# Revit family: BidetMixer_Countertop_WithPopup_Vitra_XLineSeries_A42323
name_source: partatom
category: Plumbing Fixtures
revit_build: Autodesk Revit 2017 (Build: 20160225_1515(x64)
units: mm (PartAtom-declared; Revit-internal decimal feet)

## family parameters
Cut with Voids When Loaded = No
Host = Face
OmniClass Number = 23.45.55.17
OmniClass Title = Mixing Faucets
Part Type = Normal
Room Calculation Point = No
Round Connector Dimension = Use Diameter
Shared = Yes

## types (7) — shared parameters
BIMobject category = Taps & Mixers
CW Connection = Yes
Default Elevation = 850 mm  [stored 2.78871 ft]
Depth(mm) = 167 mm  [stored 0.5479 ft]
Description = X-Line Bidet Mixer
Design country = Turkey
HW Connection = Yes
Height(mm) = 190 mm
Hot Water Supply (max.) = 80 °C
Hot Water temperature, factory set to = 38 °C
IFC Classification = Sanitary Terminal
Main Material = Brass
Manufacturer = Vitra
Manufacturer name = Vitra
Masterformat 2014 Code = 22 40 00
Masterformat 2014 Description = Plumbing Fixtures
Min. flow pressure of = 0.5 bar
MountingType = Countertop
NBS Referans Code = 45-35-70/371
NBS Referans Description = Water supply fittings for wash basins and troughs
Nominal height = 0.000
Nominal width = 0.000
Number Of Connections = 2 mm  [stored 0.00656168 ft]
OmniClass Code = 23.45.55.17
OmniClass Description = Mixing Faucets
Product Properties = Extra Water Saving, Green Building Certification, Energy Saving
Product Type = Bidet Mixer
Product certification = https://vitraglobal.com
Product family = X-Line
Product group = X-Line Bidet Mixer
Range of Hot Water Supply = 5 - 65 °C
Range of flow pressure = 1 - 5 bar
Test Pressure = 16 bar
UNSPSC Code = 301815
URL = https://vitraglobal.com
Uniclass 1.4 Code = L725111
Uniclass 1.4 Description = Mixer taps
Uniclass 2.0 Code = Pr_40_30_96_98
Uniclass 2.0 Description = Washbasin Tap
Uniclass 2015 Code = Pr_40_20_87_98
Uniclass 2015 Name = Washbasin Tap
Uniformat II Code = 22 40 00
Uniformat II Description = Plumbing Fixture
Weight Net (kg) = 2.020
Width(mm) = 50 mm  [stored 0.164042 ft]
Youtube = https://www.youtube.com
zero-valued in all types: Cost

## per-type parameters (varying)
| type | Article No. (default) | Brand | Coating Material | Color | Connection Diameter (mm) | Flow Rate(L/min. - 3 bar) | Installation instructions | Model | Product Guid | Product SKU | Product data url | Technical description | Warranty Period (Year) |
| BidetMixer-XLineSeries(Chrome)-A42323 | A42323 | Artema | Chrome | Chrome | 10 mm  [stored 0.0328084 ft] | 5L/min. |  | A42323 |  | A42323 | https://www.vitra.com.tr | https://www.vitra.com.tr | 10 Years |
| BidetMixer-XLineSeries(Gold)-A4232323 | A4232323 | Artema | Gold | Gold | 10 mm  [stored 0.0328084 ft] | 5L/min. |  | A4232323 |  | A4232323 | https://www.vitra.com.tr | https://www.vitra.com.tr | 10 Years |
| BidetMixer-XLineSeries(Chrome)-A42323EXP | A42323EXP | Vitra | Chrome | Chrome | 10 mm  [stored 0.0328084 ft] | 3L/min. | https://cdn.vitra.com.tr | A42323EXP | https://cdn.vitra.com.tr | A42323EXP | https://www.vitraglobal.com | https://www.vitraglobal.com | 7 Years |
| BidetMixer-XLineSeries(Gold)-A4232323EXP | A4232323EXP | Vitra | Gold | Gold | 10 mm  [stored 0.0328084 ft] | 3L/min. | https://cdn.vitra.com.tr | A4232323EXP | https://cdn.vitra.com.tr | A4232323EXP | https://www.vitraglobal.com | https://www.vitraglobal.com | 7 Years |
| BidetMixer-XLineSeries(Chrome)-A42323VUK | A42323VUK | Vitra | Chrome | Chrome | 15 mm  [stored 0.0492126 ft] | 3L/min. | https://cdn.vitra.com.tr | A42323VUK | https://cdn.vitra.com.tr | A42323VUK | https://www.vitraglobal.com | https://www.vitraglobal.com | 7 Years |
| BidetMixer-XLineSeries(Chrome)-A42323EKF | A42323EKF | Vitra | Chrome | Chrome | 10 mm  [stored 0.0328084 ft] | 3L/min. | https://cdn.vitra.com.tr | A42323EKF | https://cdn.vitra.com.tr | A42323EKF | https://www.vitraglobal.com | https://www.vitraglobal.com | 7 Years |
| BidetMixer-XLineSeries(Chrome)-A42323EKM | A42323EKM | Vitra | Chrome | Chrome | 10 mm  [stored 0.0328084 ft] | 3L/min. | https://cdn.vitra.com.tr | A42323EKM | https://cdn.vitra.com.tr | A42323EKM | https://www.vitraglobal.com | https://www.vitraglobal.com | 7 Years |

note: [stored X ft] marks values corroborated as IEEE doubles in the binary element streams (Revit-internal decimal feet)

## geometry (parser evidence)
native form markers: Sweep x3
no freeform markers — native parametric forms only
